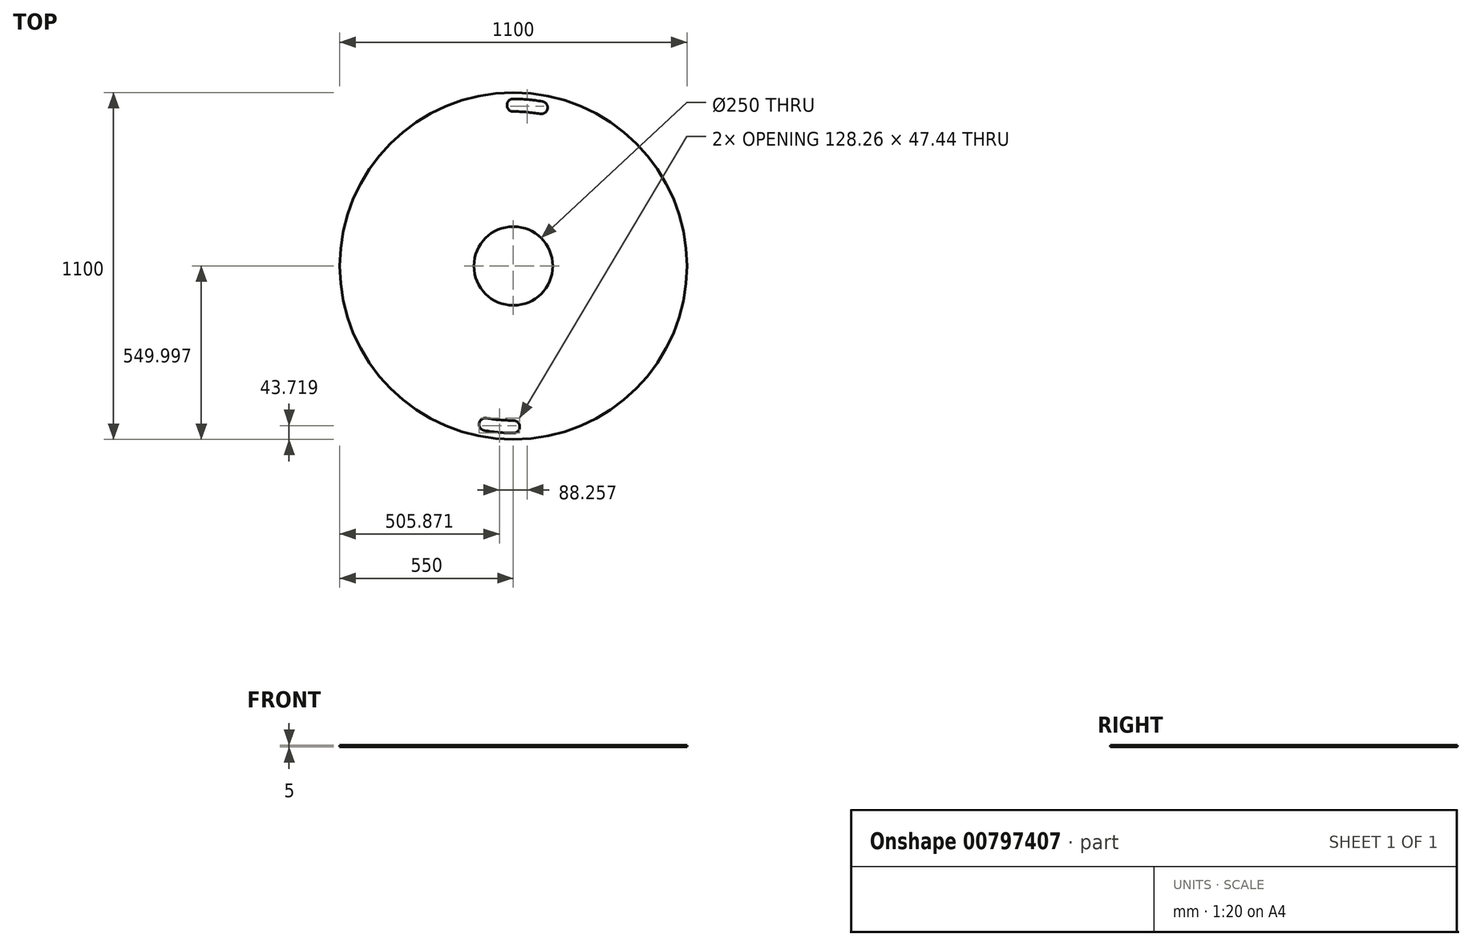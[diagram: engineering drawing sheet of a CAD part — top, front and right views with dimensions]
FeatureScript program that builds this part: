
annotation { "Feature Type Name" : "Feature", "Feature Type Description" : "" }
export const myFeature = defineFeature(function(context is Context, id is Id, definition is map)
    precondition{}
    {
        {
            var Q0;
            Q0=qCreatedBy(makeId("Top.planeOp"),FACE);
            var sketch = newSketch(context, id + "F0", { "sketchPlane" : qUnion([Q0])});
            skCircle(sketch, "E0", {"center": v(793.27, 66.52) * mm, "radius": 550 * mm});
            skCircle(sketch, "E1", {"center": v(793.27, 66.52) * mm, "radius": 125 * mm});
            skArc(sketch, "E2", {"start": v(793.27, 596.52) * mm, "mid": v(839.46, 594.5) * mm, "end": v(885.3, 588.47) * mm});
            skArc(sketch, "E3", {"start": v(878.36, 549.07) * mm, "mid": v(835.98, 554.65) * mm, "end": v(793.27, 556.52) * mm});
            skArc(sketch, "E4", {"start": v(793.27, 596.52) * mm, "mid": v(773.27, 576.52) * mm, "end": v(793.27, 556.52) * mm});
            skArc(sketch, "E5", {"start": v(878.36, 549.07) * mm, "mid": v(901.53, 565.3) * mm, "end": v(885.3, 588.47) * mm});
            skLineSegment(sketch, "E6", {"start": v(793.27, 576.52) * mm, "end": v(793.27, 66.52) * mm});
            skLineSegment(sketch, "E7", {"start": v(881.83, 568.77) * mm, "end": v(793.27, 66.52) * mm});
            skLineSegment(sketch, "E8", {"start": v(793.27, 66.52) * mm, "end": v(434.48, 66.52) * mm});
            skLineSegment(sketch, "E9", {"start": v(793.27, 66.52) * mm, "end": v(441.37, 97.3) * mm});
            skArc(sketch, "E10.MirrorCS", {"start": v(793.27, -423.48) * mm, "mid": v(813.27, -443.48) * mm, "end": v(793.27, -463.48) * mm});
            skArc(sketch, "E11.MirrorCS", {"start": v(793.27, -423.48) * mm, "mid": v(750.56, -421.62) * mm, "end": v(708.18, -416.04) * mm});
            skArc(sketch, "E12.MirrorCS", {"start": v(701.24, -455.43) * mm, "mid": v(747.08, -461.47) * mm, "end": v(793.27, -463.48) * mm});
            skArc(sketch, "E13.MirrorCS", {"start": v(701.24, -455.43) * mm, "mid": v(685.01, -432.26) * mm, "end": v(708.18, -416.04) * mm});
            skSolve(sketch);
        }
        {
            var Q0;
            Q0=makeQuery(id+"F0.imprint","IMPRINT",FACE,{"disambiguationData":[TD([[makeQuery(id+"F0.imprint","IMPRINT",EDGE,{"derivedFrom":sQuery(id+"F0.wireOp",EDGE,"E0")}),1.0]])]});
            var Q1;
            {var subQ5=sQuery(id+"F0.wireOp",EDGE,"E3");Q1=makeQuery(id+"F0.imprint","IMPRINT",FACE,{"disambiguationData":[TD([[makeQuery(id+"F0.imprint","IMPRINT",EDGE,{"derivedFrom":subQ5}),1.0]])]});}
            extrude(context, id + "F1", {"entities" : qUnion([Q0, Q1]), "depth" : 5 * mm, "offsetDistance" : 25 * mm});
        }
    });
